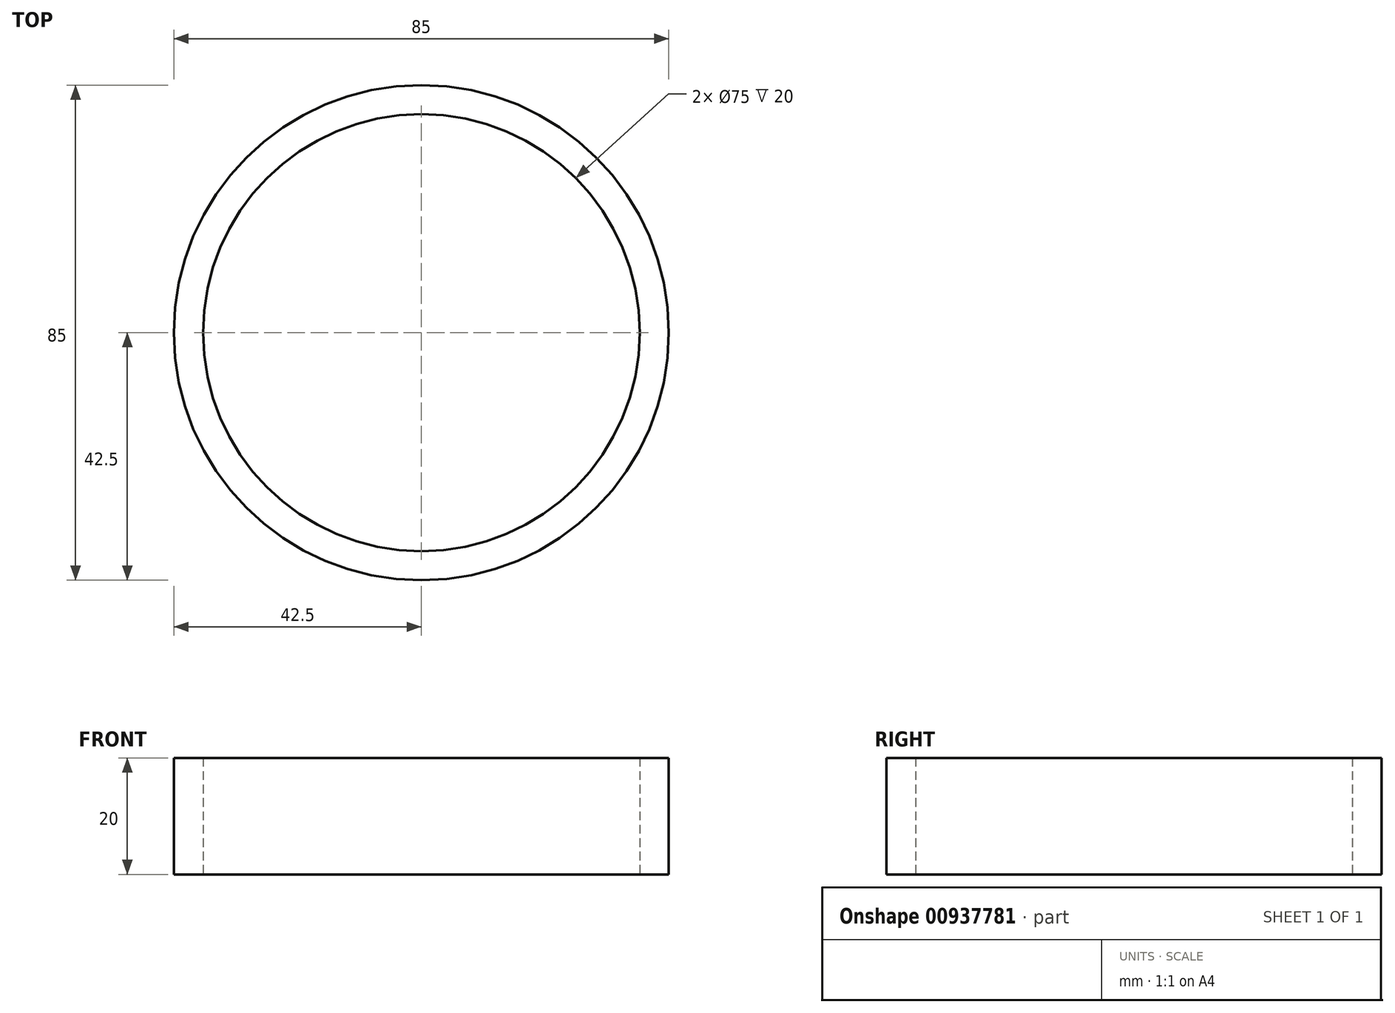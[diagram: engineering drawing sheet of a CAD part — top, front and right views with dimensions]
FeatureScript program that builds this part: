
annotation { "Feature Type Name" : "Feature", "Feature Type Description" : "" }
export const myFeature = defineFeature(function(context is Context, id is Id, definition is map)
    precondition{}
    {
        {
            var Q0;
            Q0=qCreatedBy(makeId("Top.planeOp"),FACE);
            var sketch = newSketch(context, id + "F0", { "sketchPlane" : qUnion([Q0])});
            skCircle(sketch, "E0", {"center": v(0, 0) * mm, "radius": 37.5 * mm});
            skCircle(sketch, "E1", {"center": v(0, 0) * mm, "radius": 42.5 * mm});
            skSolve(sketch);
        }
        {
            var Q0;
            Q0=qSketchRegion(id+"F0",true);
            extrude(context, id + "F1", {"entities" : qUnion([Q0]), "depth" : 20 * mm, "offsetDistance" : 25 * mm});
        }
    });
